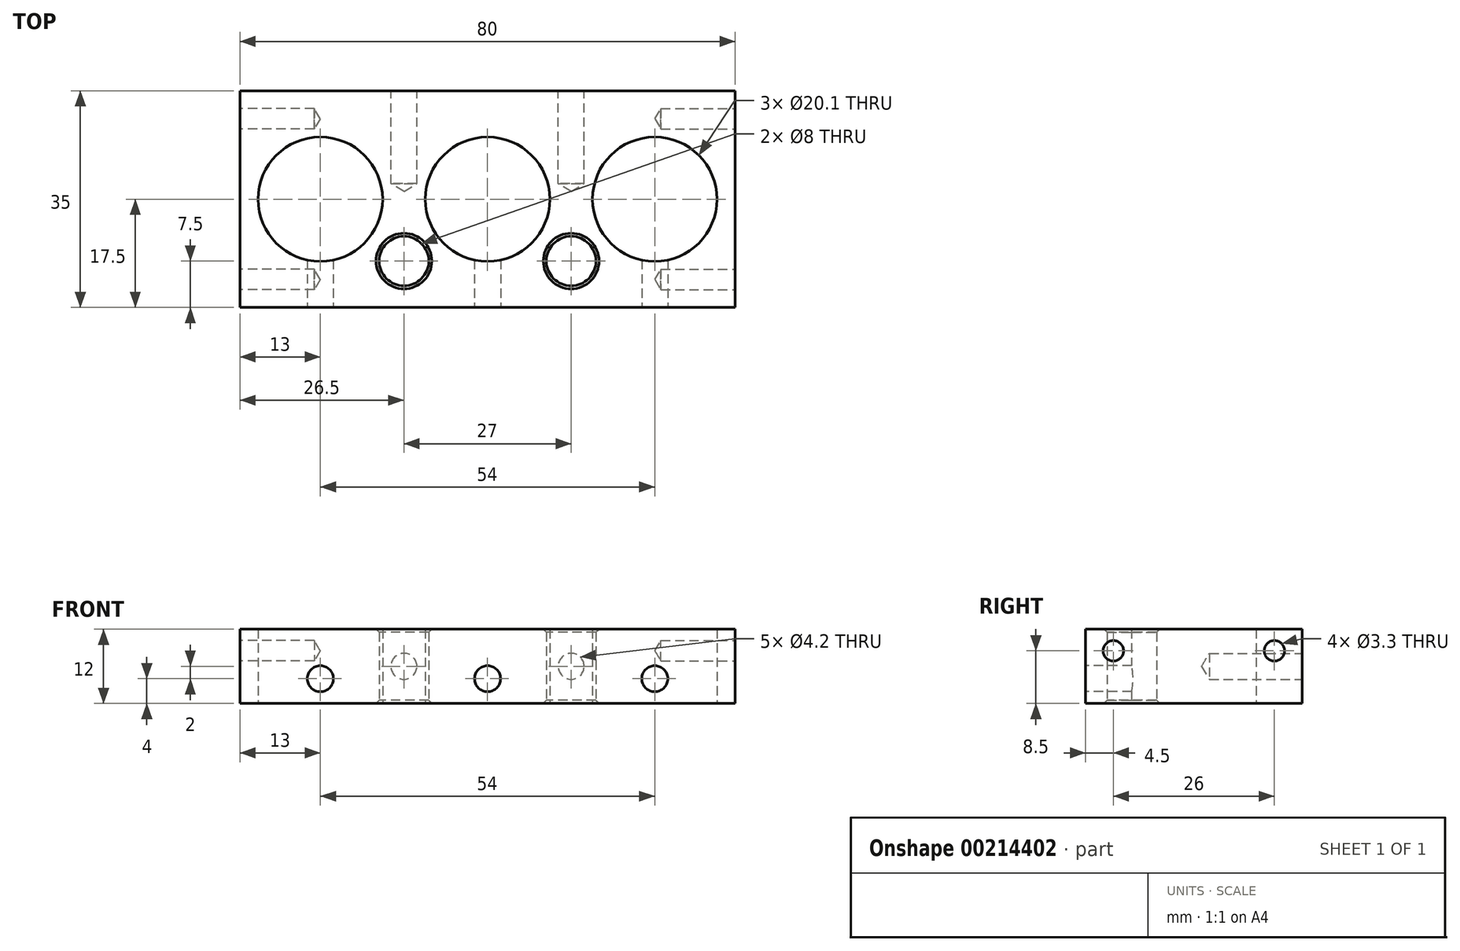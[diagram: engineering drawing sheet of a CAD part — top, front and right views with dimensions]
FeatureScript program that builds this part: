
annotation { "Feature Type Name" : "Feature", "Feature Type Description" : "" }
export const myFeature = defineFeature(function(context is Context, id is Id, definition is map)
    precondition{}
    {
        {
            var Q0;
            Q0=qCreatedBy(makeId("Top.planeOp"),FACE);
            var sketch = newSketch(context, id + "F0", { "sketchPlane" : qUnion([Q0])});
            skLineSegment(sketch, "E0.bottom", {"start": v(0, 0) * mm, "end": v(80, 0) * mm});
            skLineSegment(sketch, "E0.top", {"start": v(0, 35) * mm, "end": v(80, 35) * mm});
            skLineSegment(sketch, "E0.left", {"start": v(0, 0) * mm, "end": v(0, 35) * mm});
            skLineSegment(sketch, "E0.right", {"start": v(80, 0) * mm, "end": v(80, 35) * mm});
            skCircle(sketch, "E1", {"center": v(13, 17.5) * mm, "radius": 10.05 * mm});
            skCircle(sketch, "E2", {"center": v(67, 17.5) * mm, "radius": 10.05 * mm});
            skLineSegment(sketch, "E3", {"start": v(13, 17.5) * mm, "end": v(67, 17.5) * mm, "construction": true});
            skLineSegment(sketch, "E4", {"start": v(40, 35) * mm, "end": v(40, 17.5) * mm, "construction": true});
            skCircle(sketch, "E5", {"center": v(40, 17.5) * mm, "radius": 10.05 * mm});
            skCircle(sketch, "E6", {"center": v(26.5, 7.5) * mm, "radius": 4 * mm});
            skLineSegment(sketch, "E7", {"start": v(26.5, 7.5) * mm, "end": v(26.5, 17.5) * mm, "construction": true});
            skLineSegment(sketch, "E8", {"start": v(53.5, 17.5) * mm, "end": v(53.5, 7.5) * mm, "construction": true});
            skCircle(sketch, "E9", {"center": v(53.5, 7.5) * mm, "radius": 4 * mm});
            skSolve(sketch);
        }
        {
            var Q0;
            Q0 = qSketchRegion(id + "F0", true);
            extrude(context, id + "F1", {"entities" : qUnion([Q0]), "depth" : 12 * mm});
        }
        {
            var Q0;
            Q0=makeQuery(id+"F1.opExtrude","CAP_EDGE",EDGE,{"disambiguationData":[OSD([sQuery(id+"F0.wireOp",EDGE,"E6")])],"isStart":false});
            var Q1;
            Q1=makeQuery(id+"F1.opExtrude","CAP_EDGE",EDGE,{"disambiguationData":[OSD([sQuery(id+"F0.wireOp",EDGE,"E9")])],"isStart":false});
            var Q2;
            Q2=makeQuery(id+"F1.opExtrude","CAP_EDGE",EDGE,{"disambiguationData":[OSD([sQuery(id+"F0.wireOp",EDGE,"E9")])],"isStart":true});
            var Q3;
            Q3=makeQuery(id+"F1.opExtrude","CAP_EDGE",EDGE,{"disambiguationData":[OSD([sQuery(id+"F0.wireOp",EDGE,"E6")])],"isStart":true});
            chamfer(context, id + "F2", {"entities" : qUnion([Q0, Q1, Q2, Q3]), "width" : 0.5 * mm, "tangentPropagation" : true});
        }
        {
            var Q0;
            Q0=makeQuery(id+"F1.opExtrude","SWEPT_FACE",FACE,{"disambiguationData":[OSD([sQuery(id+"F0.wireOp",EDGE,"E0.bottom")])]});
            var sketch = newSketch(context, id + "F3", { "sketchPlane" : qUnion([Q0])});
            skLineSegment(sketch, "E10", {"start": v(0, 4) * mm, "end": v(80, 4) * mm, "construction": true});
            skCircle(sketch, "E11", {"center": v(40, 4) * mm, "radius": 2.1 * mm});
            skCircle(sketch, "E12", {"center": v(67, 4) * mm, "radius": 2.1 * mm});
            skCircle(sketch, "E13", {"center": v(13, 4) * mm, "radius": 2.1 * mm});
            skSolve(sketch);
        }
        {
            var Q0;
            Q0 = qSketchRegion(id + "F3", true);
            extrude(context, id + "F4", {"entities" : qUnion([Q0]), "operationType" : NewBodyOperationType.REMOVE, "endBound" : BoundingType.UP_TO_NEXT, "oppositeDirection" : true, "depth" : 25 * mm});
        }
        {
            var Q0;
            Q0=makeQuery(id+"F1.opExtrude","SWEPT_FACE",FACE,{"disambiguationData":[OSD([sQuery(id+"F0.wireOp",EDGE,"E0.top")])]});
            var sketch = newSketch(context, id + "F5", { "sketchPlane" : qUnion([Q0])});
            skLineSegment(sketch, "E14", {"start": v(-80, 6) * mm, "end": v(0, 6) * mm, "construction": true});
            skPoint(sketch, "E15", {"position": v(-53.5, 6) * mm});
            skPoint(sketch, "E16", {"position": v(-26.5, 6) * mm});
            skSolve(sketch);
        }
        {
            var Q0;
            Q0=sQuery(id+"F5.wireOp",VERTEX,"E15");
            var Q1;
            Q1=sQuery(id+"F5.wireOp",VERTEX,"E16");
            var Q2;
            Q2=makeQuery(id+"F1.opExtrude","SWEPT_BODY",BODY,{"disambiguationData":[OSD([sQuery(id+"F0.wireOp",EDGE,"E0.bottom"),sQuery(id+"F0.wireOp",EDGE,"E0.top"),sQuery(id+"F0.wireOp",EDGE,"E0.left"),sQuery(id+"F0.wireOp",EDGE,"E0.right"),sQuery(id+"F0.wireOp",EDGE,"E1"),sQuery(id+"F0.wireOp",EDGE,"E2"),sQuery(id+"F0.wireOp",EDGE,"E5"),sQuery(id+"F0.wireOp",EDGE,"E6"),sQuery(id+"F0.wireOp",EDGE,"E9")])]});
            hole(context, id + "F6", {"style" : HoleStyle.SIMPLE, "endStyle" : HoleEndStyle.BLIND, "standardTappedOrClearance" : lookupTablePath({ "standard" : "ISO", "engagement" : "75%", "pitch" : "0.8 mm", "size" : "M5", "type" : "Tapped" }), "standardBlindInLast" : lookupTablePath({ "standard" : "ISO", "engagement" : "75%", "pitch" : "0.8 mm", "size" : "M5", "type" : "Tapped" }), "holeDiameter" : 4.2 * mm, "holeDepth" : 15 * mm, "startFromSketch" : true, "locations" : qUnion([Q0, Q1]), "scope" : qUnion([Q2]), "majorDiameter" : 5 * mm});
        }
        {
            var Q0;
            Q0=makeQuery(id+"F1.opExtrude","SWEPT_FACE",FACE,{"disambiguationData":[OSD([sQuery(id+"F0.wireOp",EDGE,"E0.right")])]});
            var sketch = newSketch(context, id + "F7", { "sketchPlane" : qUnion([Q0])});
            skLineSegment(sketch, "E17", {"start": v(35, 8.5) * mm, "end": v(0, 8.5) * mm, "construction": true});
            skPoint(sketch, "E18", {"position": v(4.5, 8.5) * mm});
            skPoint(sketch, "E19", {"position": v(30.5, 8.5) * mm});
            skSolve(sketch);
        }
        {
            var Q0;
            Q0=sQuery(id+"F7.wireOp",VERTEX,"E18");
            var Q1;
            Q1=sQuery(id+"F7.wireOp",VERTEX,"E19");
            var Q2;
            Q2=makeQuery(id+"F1.opExtrude","SWEPT_BODY",BODY,{"disambiguationData":[OSD([sQuery(id+"F0.wireOp",EDGE,"E0.bottom"),sQuery(id+"F0.wireOp",EDGE,"E0.top"),sQuery(id+"F0.wireOp",EDGE,"E0.left"),sQuery(id+"F0.wireOp",EDGE,"E0.right"),sQuery(id+"F0.wireOp",EDGE,"E1"),sQuery(id+"F0.wireOp",EDGE,"E2"),sQuery(id+"F0.wireOp",EDGE,"E5"),sQuery(id+"F0.wireOp",EDGE,"E6"),sQuery(id+"F0.wireOp",EDGE,"E9")])]});
            hole(context, id + "F8", {"style" : HoleStyle.SIMPLE, "endStyle" : HoleEndStyle.BLIND, "standardTappedOrClearance" : lookupTablePath({ "standard" : "ISO", "engagement" : "75%", "pitch" : "0.7 mm", "size" : "M4", "type" : "Tapped" }), "standardBlindInLast" : lookupTablePath({ "standard" : "ISO", "engagement" : "75%", "pitch" : "0.7 mm", "size" : "M4", "type" : "Tapped" }), "holeDiameter" : 3.3 * mm, "holeDepth" : 12 * mm, "startFromSketch" : true, "locations" : qUnion([Q0, Q1]), "scope" : qUnion([Q2]), "majorDiameter" : 4 * mm});
        }
        {
            var Q0;
            Q0=makeQuery(id+"F1.opExtrude","SWEPT_FACE",FACE,{"disambiguationData":[OSD([sQuery(id+"F0.wireOp",EDGE,"E0.left")])]});
            var sketch = newSketch(context, id + "F9", { "sketchPlane" : qUnion([Q0])});
            skLineSegment(sketch, "E20", {"start": v(-35, 8.5) * mm, "end": v(0, 8.5) * mm, "construction": true});
            skPoint(sketch, "E21", {"position": v(-30.5, 8.5) * mm});
            skPoint(sketch, "E22", {"position": v(-4.5, 8.5) * mm});
            skSolve(sketch);
        }
        {
            var Q0;
            Q0=sQuery(id+"F9.wireOp",VERTEX,"E21");
            var Q1;
            Q1=sQuery(id+"F9.wireOp",VERTEX,"E22");
            var Q2;
            Q2=makeQuery(id+"F1.opExtrude","SWEPT_BODY",BODY,{"disambiguationData":[OSD([sQuery(id+"F0.wireOp",EDGE,"E0.bottom"),sQuery(id+"F0.wireOp",EDGE,"E0.top"),sQuery(id+"F0.wireOp",EDGE,"E0.left"),sQuery(id+"F0.wireOp",EDGE,"E0.right"),sQuery(id+"F0.wireOp",EDGE,"E1"),sQuery(id+"F0.wireOp",EDGE,"E2"),sQuery(id+"F0.wireOp",EDGE,"E5"),sQuery(id+"F0.wireOp",EDGE,"E6"),sQuery(id+"F0.wireOp",EDGE,"E9")])]});
            hole(context, id + "F10", {"style" : HoleStyle.SIMPLE, "endStyle" : HoleEndStyle.BLIND, "standardTappedOrClearance" : lookupTablePath({ "standard" : "ISO", "engagement" : "75%", "pitch" : "0.7 mm", "size" : "M4", "type" : "Tapped" }), "standardBlindInLast" : lookupTablePath({ "standard" : "ISO", "engagement" : "75%", "pitch" : "0.7 mm", "size" : "M4", "type" : "Tapped" }), "holeDiameter" : 3.3 * mm, "holeDepth" : 12 * mm, "startFromSketch" : true, "locations" : qUnion([Q0, Q1]), "scope" : qUnion([Q2]), "majorDiameter" : 4 * mm});
        }
    });
